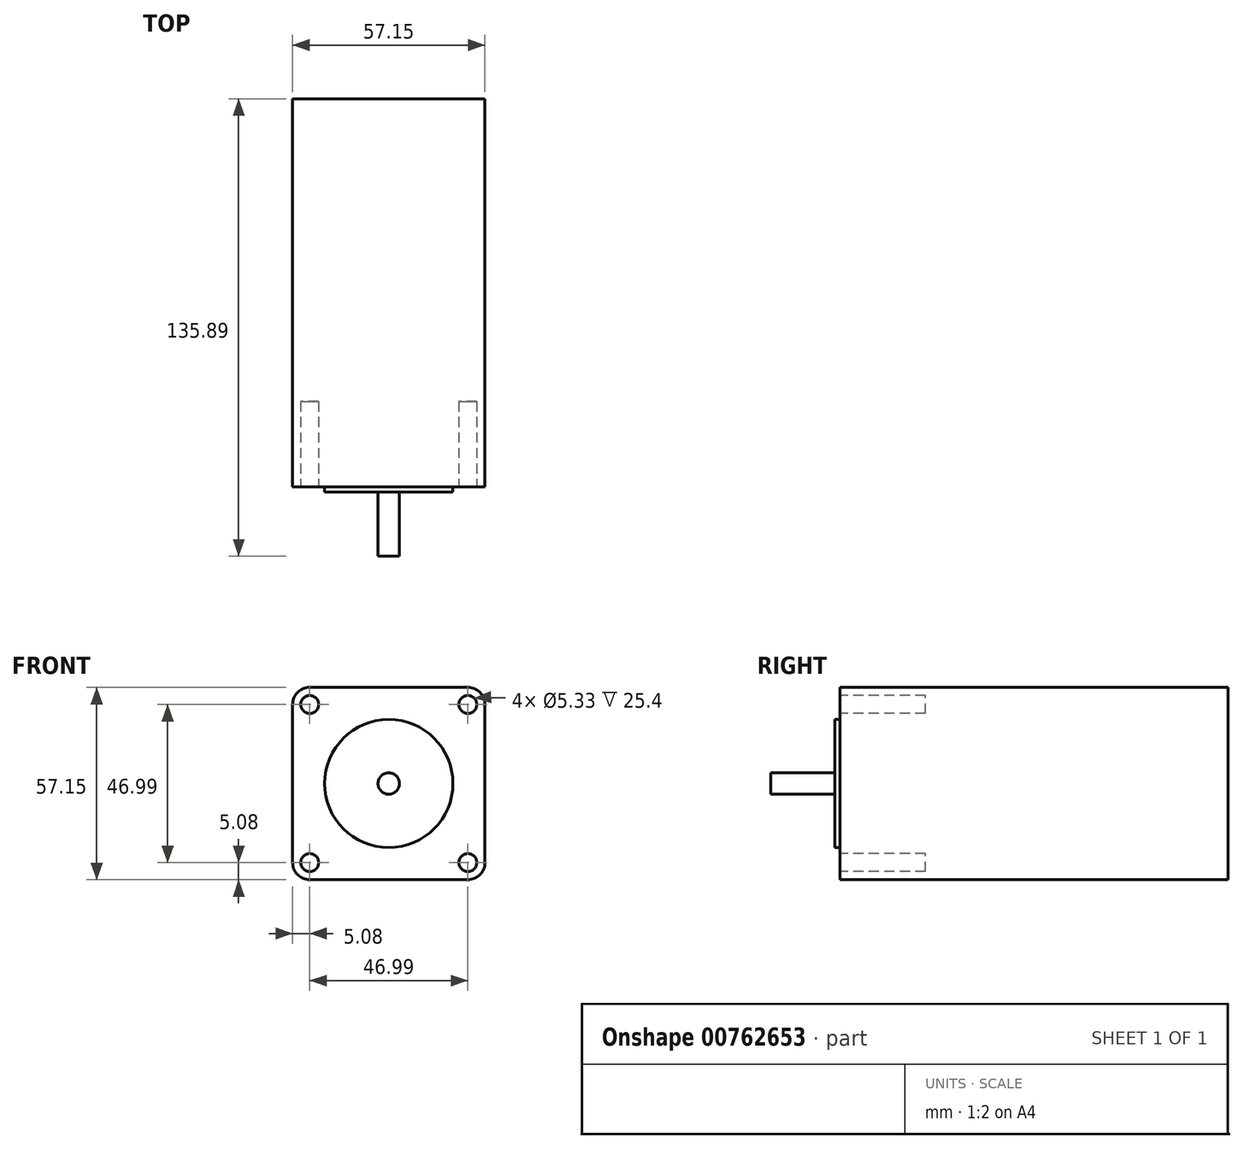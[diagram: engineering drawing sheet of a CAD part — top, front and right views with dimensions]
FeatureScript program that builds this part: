
annotation { "Feature Type Name" : "Feature", "Feature Type Description" : "" }
export const myFeature = defineFeature(function(context is Context, id is Id, definition is map)
    precondition{}
    {
        {
            var Q0;
            Q0=qCreatedBy(makeId("Front.planeOp"),FACE);
            var sketch = newSketch(context, id + "F0", { "sketchPlane" : qUnion([Q0])});
            skLineSegment(sketch, "E0.bottom", {"start": v(0, 0) * mm, "end": v(57.15, 0) * mm});
            skLineSegment(sketch, "E0.top", {"start": v(0, 57.15) * mm, "end": v(57.15, 57.15) * mm});
            skLineSegment(sketch, "E0.left", {"start": v(0, 0) * mm, "end": v(0, 57.15) * mm});
            skLineSegment(sketch, "E0.right", {"start": v(57.15, 0) * mm, "end": v(57.15, 57.15) * mm});
            skSolve(sketch);
        }
        {
            var Q0;
            Q0 = qSketchRegion(id + "F0", true);
            extrude(context, id + "F1", {"entities" : qUnion([Q0]), "depth" : 115.32 * mm, "offsetDistance" : 25.4 * mm});
        }
        {
            var Q0;
            Q0=makeQuery(id+"F1.opExtrude","SWEPT_EDGE",EDGE,{"disambiguationData":[OSD([sQuery(id+"F0.wireOp",EDGE,"E0.top"),sQuery(id+"F0.wireOp",EDGE,"E0.right")])]});
            var Q1;
            Q1=makeQuery(id+"F1.opExtrude","SWEPT_EDGE",EDGE,{"disambiguationData":[OSD([sQuery(id+"F0.wireOp",EDGE,"E0.bottom"),sQuery(id+"F0.wireOp",EDGE,"E0.right")])]});
            var Q2;
            Q2=makeQuery(id+"F1.opExtrude","SWEPT_EDGE",EDGE,{"disambiguationData":[OSD([sQuery(id+"F0.wireOp",EDGE,"E0.bottom"),sQuery(id+"F0.wireOp",EDGE,"E0.left")])]});
            var Q3;
            Q3=makeQuery(id+"F1.opExtrude","SWEPT_EDGE",EDGE,{"disambiguationData":[OSD([sQuery(id+"F0.wireOp",EDGE,"E0.top"),sQuery(id+"F0.wireOp",EDGE,"E0.left")])]});
            fillet(context, id + "F2", {"entities" : qUnion([Q0, Q1, Q2, Q3]), "radius" : 5.08 * mm, "tangentPropagation" : true, "allowEdgeOverflow" : false});
        }
        {
            var Q0;
            Q0=makeQuery(id+"F1.opExtrude","CAP_FACE",FACE,{"disambiguationData":[OSD([sQuery(id+"F0.wireOp",EDGE,"E0.bottom"),sQuery(id+"F0.wireOp",EDGE,"E0.top"),sQuery(id+"F0.wireOp",EDGE,"E0.left"),sQuery(id+"F0.wireOp",EDGE,"E0.right")])],"isStart":false});
            var sketch = newSketch(context, id + "F3", { "sketchPlane" : qUnion([Q0])});
            skCircle(sketch, "E1", {"center": v(28.58, 28.58) * mm, "radius": 19.05 * mm});
            skPoint(sketch, "E1.centerSnap0", {"position": v(28.58, 57.15) * mm});
            skPoint(sketch, "E1.centerSnap1", {"position": v(0, 28.58) * mm});
            skSolve(sketch);
        }
        {
            var Q0;
            Q0 = qSketchRegion(id + "F3", true);
            extrude(context, id + "F4", {"entities" : qUnion([Q0]), "operationType" : NewBodyOperationType.ADD, "depth" : 1.52 * mm, "offsetDistance" : 25.4 * mm});
        }
        {
            var Q0;
            Q0=makeQuery(id+"F4.opExtrude","CAP_FACE",FACE,{"disambiguationData":[OSD([sQuery(id+"F3.wireOp",EDGE,"E1")])],"isStart":false});
            var sketch = newSketch(context, id + "F5", { "sketchPlane" : qUnion([Q0])});
            skCircle(sketch, "E2", {"center": v(28.58, 28.58) * mm, "radius": 3.18 * mm});
            skSolve(sketch);
        }
        {
            var Q0;
            Q0 = qSketchRegion(id + "F5", true);
            extrude(context, id + "F6", {"entities" : qUnion([Q0]), "operationType" : NewBodyOperationType.ADD, "depth" : 19.05 * mm, "offsetDistance" : 25.4 * mm});
        }
        {
            var Q0;
            Q0=makeQuery(id+"F1.opExtrude","CAP_FACE",FACE,{"disambiguationData":[OSD([sQuery(id+"F0.wireOp",EDGE,"E0.bottom"),sQuery(id+"F0.wireOp",EDGE,"E0.top"),sQuery(id+"F0.wireOp",EDGE,"E0.left"),sQuery(id+"F0.wireOp",EDGE,"E0.right")])],"isStart":false});
            var sketch = newSketch(context, id + "F7", { "sketchPlane" : qUnion([Q0])});
            skCircle(sketch, "E3", {"center": v(28.58, 28.58) * mm, "radius": 33.34 * mm, "construction": true});
            skLineSegment(sketch, "E4", {"start": v(0, 28.58) * mm, "end": v(57.15, 28.58) * mm, "construction": true});
            skCircle(sketch, "E5", {"center": v(52.07, 52.07) * mm, "radius": 2.67 * mm});
            skCircle(sketch, "E6", {"center": v(5.08, 52.07) * mm, "radius": 2.67 * mm});
            skCircle(sketch, "E7.MirrorC", {"center": v(52.07, 5.08) * mm, "radius": 2.67 * mm});
            skCircle(sketch, "E8.MirrorC", {"center": v(5.08, 5.08) * mm, "radius": 2.67 * mm});
            skSolve(sketch);
        }
        {
            var Q0;
            Q0 = qSketchRegion(id + "F7", true);
            extrude(context, id + "F8", {"entities" : qUnion([Q0]), "operationType" : NewBodyOperationType.REMOVE, "oppositeDirection" : true, "depth" : 25.4 * mm, "offsetDistance" : 25.4 * mm});
        }
    });
